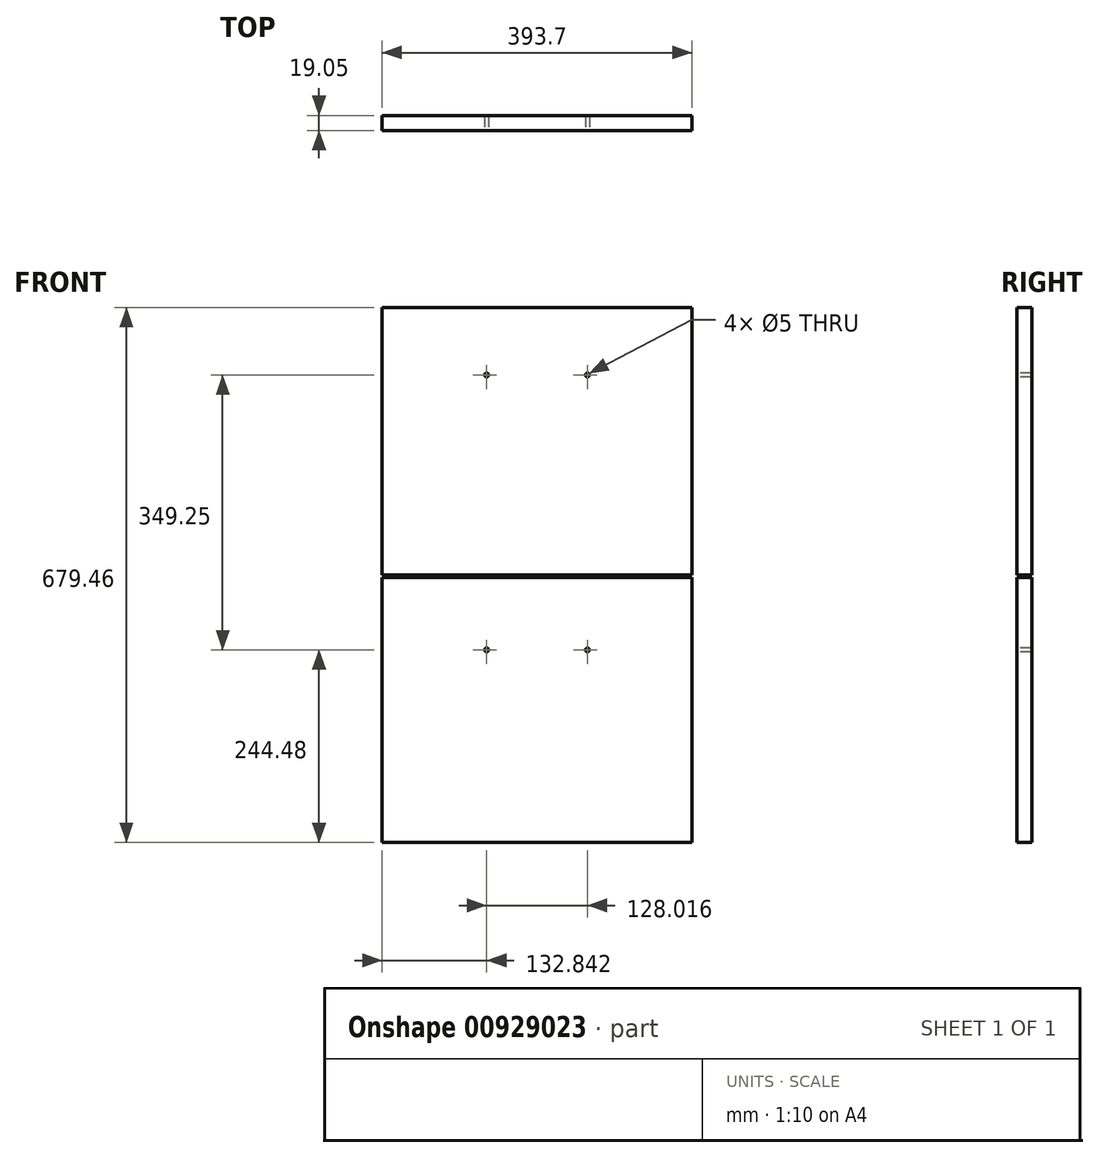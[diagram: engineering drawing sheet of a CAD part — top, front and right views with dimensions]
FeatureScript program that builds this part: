
annotation { "Feature Type Name" : "Feature", "Feature Type Description" : "" }
export const myFeature = defineFeature(function(context is Context, id is Id, definition is map)
    precondition{}
    {
        {
            var Q0;
            Q0=qCreatedBy(makeId("Front.planeOp"),FACE);
            var sketch = newSketch(context, id + "F0", { "sketchPlane" : qUnion([Q0])});
            skLineSegment(sketch, "E0.bottom", {"start": v(196.85, 339.73) * mm, "end": v(-196.85, 339.73) * mm});
            skLineSegment(sketch, "E0.top", {"start": v(196.85, -339.73) * mm, "end": v(-196.85, -339.73) * mm});
            skLineSegment(sketch, "E0.left", {"start": v(196.85, 339.73) * mm, "end": v(196.85, -339.73) * mm});
            skLineSegment(sketch, "E0.right", {"start": v(-196.85, 339.73) * mm, "end": v(-196.85, -339.73) * mm});
            skPoint(sketch, "E0.middle", {"position": v(0, 0) * mm});
            skSolve(sketch);
        }
        {
            var Q0;
            Q0=makeQuery(id+"F0.imprint","IMPRINT",FACE,{"disambiguationData":[TD([[makeQuery(id+"F0.imprint","IMPRINT",EDGE,{"derivedFrom":sQuery(id+"F0.wireOp",EDGE,"E0.bottom")}),1.0]])]});
            extrude(context, id + "F1", {"entities" : qUnion([Q0]), "depth" : 19.05 * mm, "offsetDistance" : 25.4 * mm});
        }
        {
            var Q0;
            Q0=makeQuery(id+"F1.opExtrude","CAP_FACE",FACE,{"disambiguationData":[OSD([sQuery(id+"F0.wireOp",EDGE,"E0.bottom"),sQuery(id+"F0.wireOp",EDGE,"E0.top"),sQuery(id+"F0.wireOp",EDGE,"E0.left"),sQuery(id+"F0.wireOp",EDGE,"E0.right")])],"isStart":false});
            var sketch = newSketch(context, id + "F2", { "sketchPlane" : qUnion([Q0])});
            skLineSegment(sketch, "E1", {"start": v(-196.85, -339.73) * mm, "end": v(-196.85, -3.17) * mm});
            skLineSegment(sketch, "E2", {"start": v(-196.85, -3.17) * mm, "end": v(196.85, -3.17) * mm});
            skLineSegment(sketch, "E3", {"start": v(-196.85, -3.17) * mm, "end": v(-196.85, 0) * mm});
            skLineSegment(sketch, "E4", {"start": v(-196.85, 0) * mm, "end": v(196.85, 0) * mm});
            skLineSegment(sketch, "E5.left", {"start": v(196.85, 168.28) * mm, "end": v(196.85, 165.1) * mm});
            skLineSegment(sketch, "E5.right", {"start": v(-196.85, 168.28) * mm, "end": v(-196.85, 165.1) * mm});
            skPoint(sketch, "E5.middle", {"position": v(0, 166.69) * mm});
            skSolve(sketch);
        }
        {
            var Q0;
            Q0=makeQuery(id+"F2.imprint","IMPRINT",FACE,{"disambiguationData":[TD([[makeQuery(id+"F2.imprint","IMPRINT",EDGE,{"derivedFrom":sQuery(id+"F2.wireOp",EDGE,"E5.bottom")}),1.0]])]});
            var Q1;
            {var subQ0=sQuery(id+"F2.wireOp",EDGE,"E2");Q1=makeQuery(id+"F2.imprint","IMPRINT",FACE,{"disambiguationData":[TD([[makeQuery(id+"F2.imprint","IMPRINT",EDGE,{"derivedFrom":subQ0}),1.0]])]});}
            extrude(context, id + "F3", {"entities" : qUnion([Q0, Q1]), "operationType" : NewBodyOperationType.REMOVE, "oppositeDirection" : true, "depth" : 25.4 * mm, "offsetDistance" : 25.4 * mm});
        }
        {
            var Q0;
            {var subQ0=sQuery(id+"F0.wireOp",EDGE,"E0.bottom");var subQ1=sQuery(id+"F0.wireOp",EDGE,"E0.right");var subQ2=sQuery(id+"F0.wireOp",EDGE,"E0.left");Q0=makeQuery(id+"F3.boolean.opBoolean","SPLIT",FACE,{"disambiguationData":[TD([makeQuery(id+"F1.opExtrude","SWEPT_FACE",FACE,{"disambiguationData":[OSD([subQ0])]})])],"derivedFrom":makeQuery(id+"F1.opExtrude","CAP_FACE",FACE,{"disambiguationData":[OSD([subQ0,sQuery(id+"F0.wireOp",EDGE,"E0.top"),subQ2,subQ1])],"isStart":false})});}
            var sketch = newSketch(context, id + "F4", { "sketchPlane" : qUnion([Q0])});
            skPoint(sketch, "E6.startSnap0", {"position": v(-196.85, 169.86) * mm});
            skPoint(sketch, "E6.startSnap1", {"position": v(0, 339.73) * mm});
            skLineSegment(sketch, "E7", {"start": v(0, 339.73) * mm, "end": v(0, 254) * mm});
            skLineSegment(sketch, "E8", {"start": v(0, 254) * mm, "end": v(64, 254) * mm});
            skLineSegment(sketch, "E9", {"start": v(64, 254) * mm, "end": v(-64, 254) * mm});
            skSolve(sketch);
        }
        {
            var Q0;
            Q0=sQuery(id+"F4.wireOp",VERTEX,"E6.end");
            var Q1;
            Q1=sQuery(id+"F4.wireOp",VERTEX,"khDCiakj-hvbn-O7Iq-0KTA-B93rkDrHPvJp.end");
            var Q2;
            Q2=sQuery(id+"F4.wireOp",VERTEX,"E9.end");
            var Q3;
            Q3=sQuery(id+"F4.wireOp",VERTEX,"E8.end");
            var Q4;
            Q4=makeQuery(id+"F3.boolean.opBoolean","SPLIT",BODY,{"disambiguationData":[OD(0.0)],"derivedFrom":makeQuery(id+"F1.opExtrude","SWEPT_BODY",BODY,{"disambiguationData":[OSD([sQuery(id+"F0.wireOp",EDGE,"E0.bottom"),sQuery(id+"F0.wireOp",EDGE,"E0.top"),sQuery(id+"F0.wireOp",EDGE,"E0.left"),sQuery(id+"F0.wireOp",EDGE,"E0.right")])]})});
            hole(context, id + "F5", {"style" : HoleStyle.SIMPLE, "endStyle" : HoleEndStyle.THROUGH, "holeDiameter" : 5 * mm, "majorDiameter" : 6.35 * mm, "isTappedThrough" : true, "tappedDepth" : 12.7 * mm, "tapClearance" : 3, "startFromSketch" : true, "locations" : qUnion([Q0, Q1, Q2, Q3]), "scope" : qUnion([Q4])});
        }
        {
            var Q0;
            {var subQ0=sQuery(id+"F0.wireOp",EDGE,"E0.top");var subQ1=sQuery(id+"F0.wireOp",EDGE,"E0.left");var subQ2=sQuery(id+"F0.wireOp",EDGE,"E0.right");Q0=makeQuery(id+"F3.boolean.opBoolean","SPLIT",FACE,{"disambiguationData":[TD([makeQuery(id+"F1.opExtrude","SWEPT_FACE",FACE,{"disambiguationData":[OSD([subQ0])]})])],"derivedFrom":makeQuery(id+"F1.opExtrude","CAP_FACE",FACE,{"disambiguationData":[OSD([sQuery(id+"F0.wireOp",EDGE,"E0.bottom"),subQ0,subQ1,subQ2])],"isStart":false})});}
            var sketch = newSketch(context, id + "F6", { "sketchPlane" : qUnion([Q0])});
            skLineSegment(sketch, "E10", {"start": v(0, -3.17) * mm, "end": v(0, -95.25) * mm});
            skLineSegment(sketch, "E11", {"start": v(0, -95.25) * mm, "end": v(64, -95.25) * mm});
            skLineSegment(sketch, "E12", {"start": v(64, -95.25) * mm, "end": v(-64, -95.25) * mm});
            skPoint(sketch, "E12.endSnap0", {"position": v(32, -95.25) * mm});
            skSolve(sketch);
        }
        {
            var Q0;
            Q0=sQuery(id+"F6.wireOp",VERTEX,"E11.end");
            var Q1;
            Q1=sQuery(id+"F6.wireOp",VERTEX,"E12.end");
            var Q2;
            Q2=makeQuery(id+"F3.boolean.opBoolean","SPLIT",BODY,{"disambiguationData":[OD(1.0)],"derivedFrom":makeQuery(id+"F1.opExtrude","SWEPT_BODY",BODY,{"disambiguationData":[OSD([sQuery(id+"F0.wireOp",EDGE,"E0.bottom"),sQuery(id+"F0.wireOp",EDGE,"E0.top"),sQuery(id+"F0.wireOp",EDGE,"E0.left"),sQuery(id+"F0.wireOp",EDGE,"E0.right")])]})});
            hole(context, id + "F7", {"style" : HoleStyle.SIMPLE, "endStyle" : HoleEndStyle.THROUGH, "holeDiameter" : 5 * mm, "majorDiameter" : 6.35 * mm, "isTappedThrough" : true, "tappedDepth" : 12.7 * mm, "tapClearance" : 3, "startFromSketch" : true, "locations" : qUnion([Q0, Q1]), "scope" : qUnion([Q2])});
        }
    });
